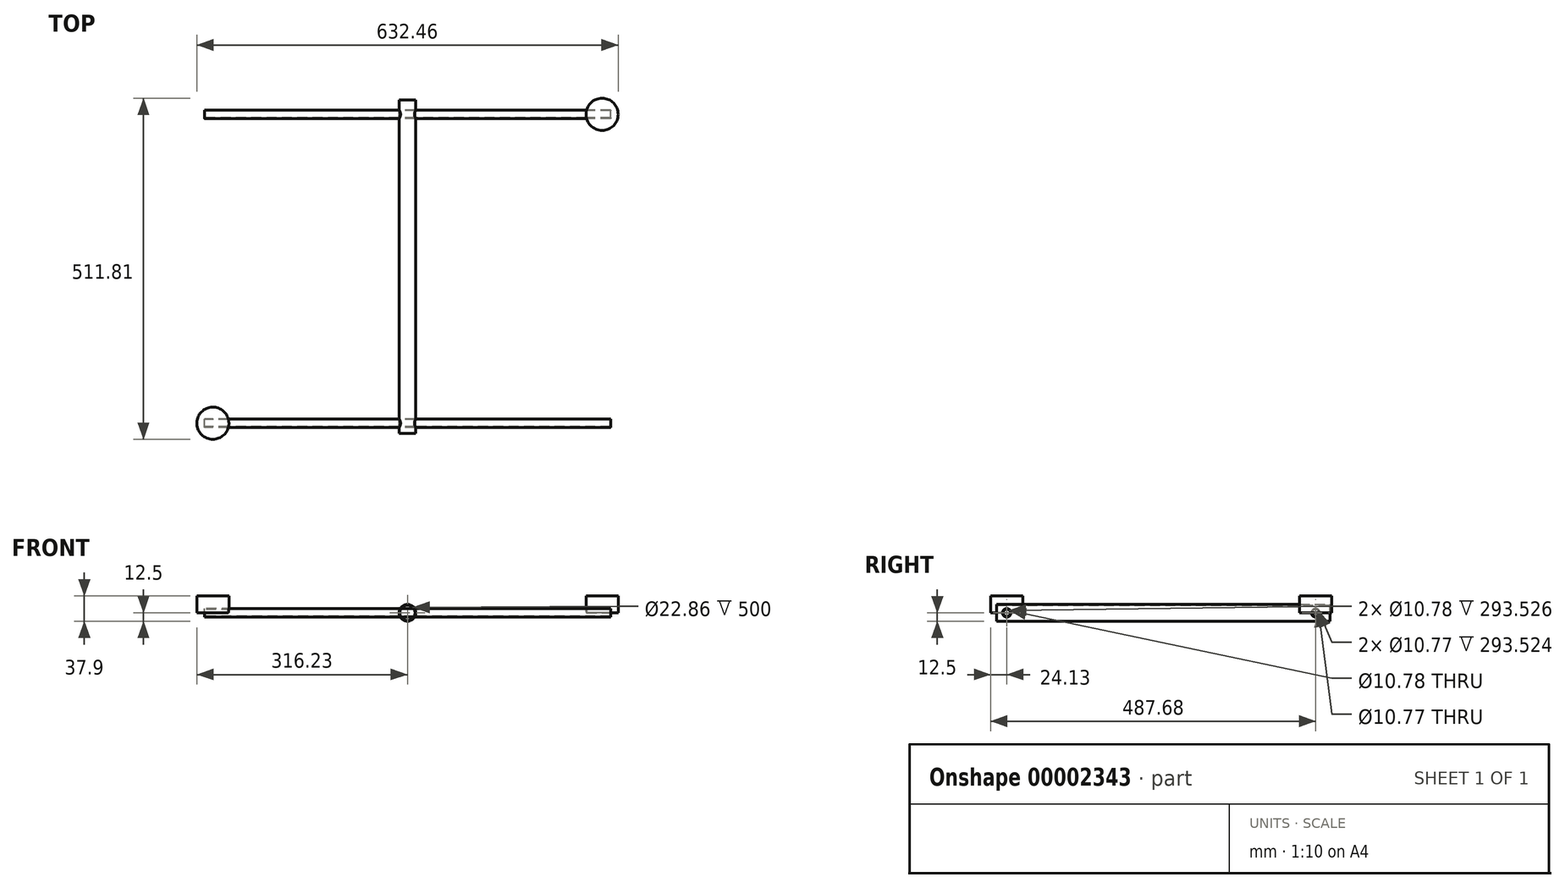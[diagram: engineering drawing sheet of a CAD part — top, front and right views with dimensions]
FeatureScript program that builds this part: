
annotation { "Feature Type Name" : "Feature", "Feature Type Description" : "" }
export const myFeature = defineFeature(function(context is Context, id is Id, definition is map)
    precondition{}
    {
        {
            var Q0;
            Q0=qCreatedBy(makeId("Front.planeOp"),FACE);
            var sketch = newSketch(context, id + "F0", { "sketchPlane" : qUnion([Q0])});
            skCircle(sketch, "E0", {"center": v(0, 0) * mm, "radius": 11.43 * mm});
            skCircle(sketch, "E1", {"center": v(0, 0) * mm, "radius": 12.5 * mm});
            skSolve(sketch);
        }
        {
            var Q0;
            Q0=makeQuery(id+"F0.imprint","IMPRINT",FACE,{"disambiguationData":[TD([[makeQuery(id+"F0.imprint","IMPRINT",EDGE,{"derivedFrom":sQuery(id+"F0.wireOp",EDGE,"E0")}),-1.0]])]});
            extrude(context, id + "F1", {"entities" : qUnion([Q0]), "endBound" : BoundingType.SYMMETRIC, "depth" : 500 * mm});
        }
        {
            var Q0;
            Q0=qCreatedBy(makeId("Right.planeOp"),FACE);
            var sketch = newSketch(context, id + "F2", { "sketchPlane" : qUnion([Q0])});
            skCircle(sketch, "E2", {"center": v(-234.95, 0) * mm, "radius": 6.35 * mm});
            skCircle(sketch, "E3", {"center": v(-234.95, 0) * mm, "radius": 5.4 * mm});
            skCircle(sketch, "E4", {"center": v(228.6, 0) * mm, "radius": 6.35 * mm});
            skCircle(sketch, "E5", {"center": v(228.6, 0) * mm, "radius": 5.38 * mm});
            skSolve(sketch);
        }
        {
            var Q0;
            Q0=qCreatedBy(makeId("Top.planeOp"),FACE);
            var sketch = newSketch(context, id + "F3", { "sketchPlane" : qUnion([Q0])});
            skCircle(sketch, "E6", {"center": v(292.1, 228.6) * mm, "radius": 24.13 * mm});
            skCircle(sketch, "E7.0.MirrorC", {"center": v(-292.1, 228.6) * mm, "radius": 24.13 * mm});
            skCircle(sketch, "E8.0.MirrorC", {"center": v(292.1, -234.95) * mm, "radius": 24.13 * mm});
            skCircle(sketch, "E9.0.MirrorC", {"center": v(-292.1, -234.95) * mm, "radius": 24.13 * mm});
            skSolve(sketch);
        }
        {
            var Q0;
            {Q0=qUnion([makeQuery(id+"F2.imprint","IMPRINT",FACE,{"disambiguationData":[TD([[makeQuery(id+"F2.imprint","IMPRINT",EDGE,{"derivedFrom":sQuery(id+"F2.wireOp",EDGE,"E2")}),1.0]])]}),makeQuery(id+"F2.imprint","IMPRINT",FACE,{"disambiguationData":[TD([[makeQuery(id+"F2.imprint","IMPRINT",EDGE,{"derivedFrom":sQuery(id+"F2.wireOp",EDGE,"E4")}),1.0]])]})]);}
            extrude(context, id + "F4", {"entities" : qUnion([Q0]), "operationType" : NewBodyOperationType.ADD, "endBound" : BoundingType.SYMMETRIC, "depth" : 609.6 * mm});
        }
        {
            var Q0;
            {Q0=qUnion([makeQuery(id+"F3.imprint","IMPRINT",FACE,{"disambiguationData":[TD([[makeQuery(id+"F3.imprint","IMPRINT",EDGE,{"derivedFrom":sQuery(id+"F3.wireOp",EDGE,"E6")}),1.0]])]}),makeQuery(id+"F3.imprint","IMPRINT",FACE,{"disambiguationData":[TD([[makeQuery(id+"F3.imprint","IMPRINT",EDGE,{"derivedFrom":sQuery(id+"F3.wireOp",EDGE,"E7.0.MirrorC")}),-1.0]])]}),makeQuery(id+"F3.imprint","IMPRINT",FACE,{"disambiguationData":[TD([[makeQuery(id+"F3.imprint","IMPRINT",EDGE,{"derivedFrom":sQuery(id+"F3.wireOp",EDGE,"E8.0.MirrorC")}),-1.0]])]}),makeQuery(id+"F3.imprint","IMPRINT",FACE,{"disambiguationData":[TD([[makeQuery(id+"F3.imprint","IMPRINT",EDGE,{"derivedFrom":sQuery(id+"F3.wireOp",EDGE,"E9.0.MirrorC")}),1.0]])]})]);}
            extrude(context, id + "F5", {"entities" : qUnion([Q0]), "operationType" : NewBodyOperationType.ADD, "depth" : 25.4 * mm});
        }
    });
